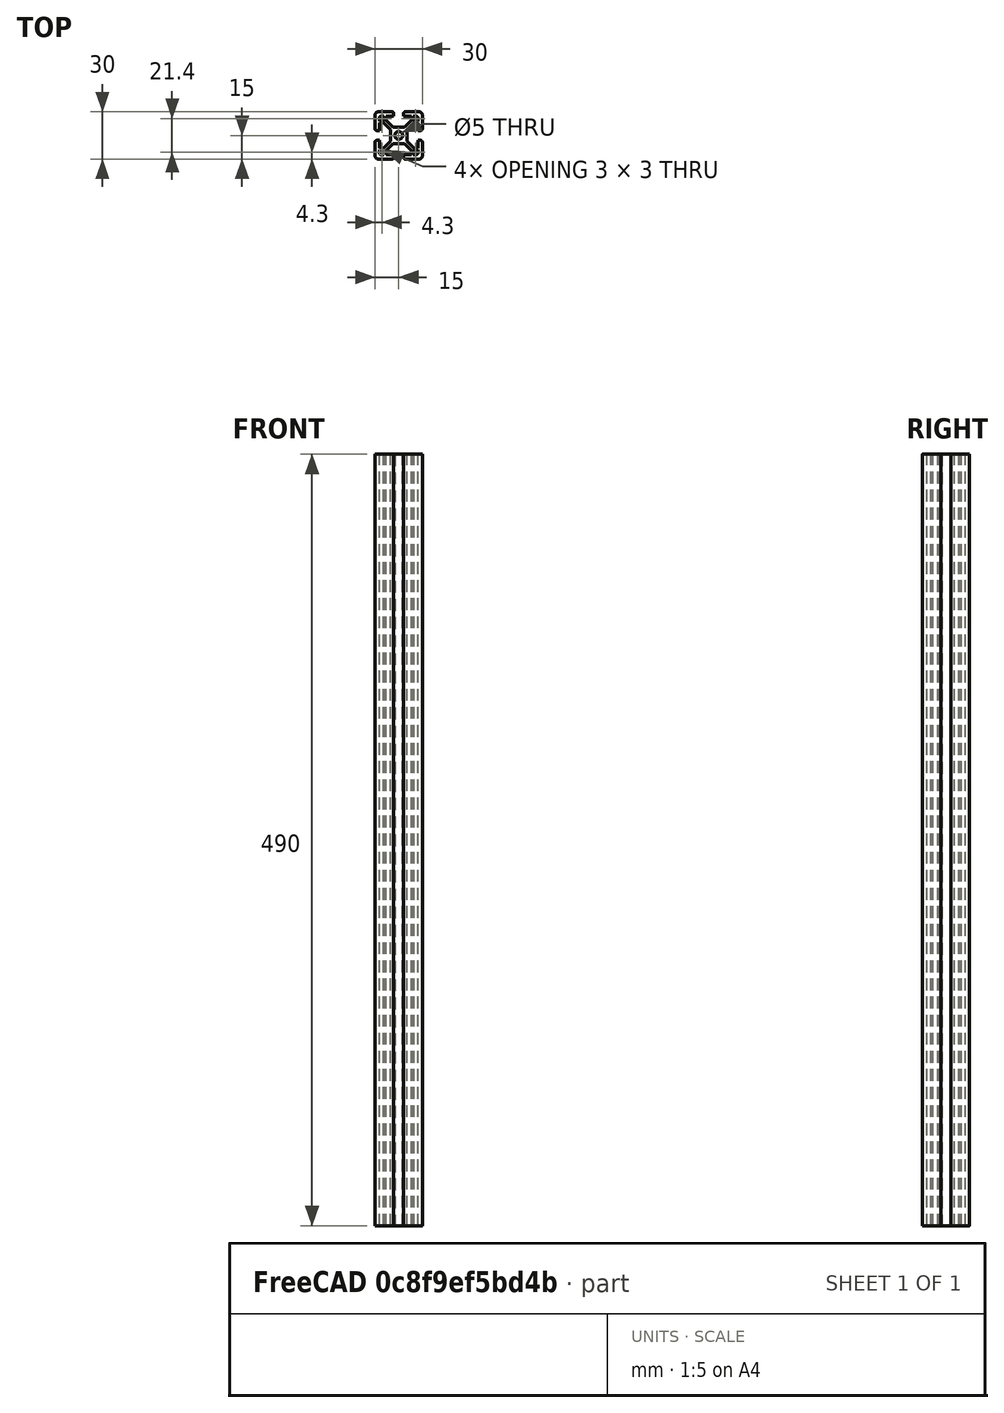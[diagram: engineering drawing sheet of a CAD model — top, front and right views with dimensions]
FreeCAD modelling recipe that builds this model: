
FCSTD DOCUMENT  (FreeCAD 0.19R18353 (Git))
Label: Profile_3030-490
License: CreativeCommons Attribution
LicenseURL: http://creativecommons.org/licenses/by/4.0/
objects: Sketcher::SketchObject×1, PartDesign::Pad×1, PartDesign::Body×1
note: 4 computed .brp shape members not serialized (recipe doc carries the construction recipe); baked Part::Feature solids carry a one-line shape summary decoded from their .brp

FEATURE [Sketcher::SketchObject] Sketch
  MapMode = 5
  Support = -> [XY_Plane]
  sketch-geometry (137):
    g0: LineSegment [constr] StartX=-5.2 StartY=5.2 StartZ=0 EndX=5.2 EndY=5.2 EndZ=0
    g1: LineSegment [constr] StartX=5.2 StartY=5.2 StartZ=0 EndX=5.2 EndY=-5.2 EndZ=0
    g2: LineSegment [constr] StartX=5.2 StartY=-5.2 StartZ=0 EndX=-5.2 EndY=-5.2 EndZ=0
    g3: LineSegment [constr] StartX=-5.2 StartY=-5.2 StartZ=0 EndX=-5.2 EndY=5.2 EndZ=0
    g4: LineSegment [constr] StartX=-15 StartY=15 StartZ=0 EndX=15 EndY=15 EndZ=0
    g5: LineSegment [constr] StartX=15 StartY=15 StartZ=0 EndX=15 EndY=-15 EndZ=0
    g6: LineSegment [constr] StartX=15 StartY=-15 StartZ=0 EndX=-15 EndY=-15 EndZ=0
    g7: LineSegment [constr] StartX=-15 StartY=-15 StartZ=0 EndX=-15 EndY=15 EndZ=0
    g8: LineSegment [constr] StartX=-12.2 StartY=12.2 StartZ=0 EndX=12.2 EndY=12.2 EndZ=0
    g9: LineSegment [constr] StartX=12.2 StartY=12.2 StartZ=0 EndX=12.2 EndY=-12.2 EndZ=0
    g10: LineSegment [constr] StartX=12.2 StartY=-12.2 StartZ=0 EndX=-12.2 EndY=-12.2 EndZ=0
    g11: LineSegment [constr] StartX=-12.2 StartY=-12.2 StartZ=0 EndX=-12.2 EndY=12.2 EndZ=0
    g12: Circle CenterX=0 CenterY=0 CenterZ=0 NormalX=0 NormalY=0 NormalZ=1 AngleXU=0 Radius=2.5
    g13: LineSegment [constr] StartX=15 StartY=15 StartZ=0 EndX=5.2 EndY=5.2 EndZ=0
    g14: LineSegment [constr] StartX=13.5151 StartY=15 StartZ=0 EndX=15 EndY=13.5151 EndZ=0
    g15: LineSegment [constr] StartX=15 StartY=13.5151 StartZ=0 EndX=5.2 EndY=3.71508 EndZ=0
    g16: LineSegment [constr] StartX=5.2 StartY=3.71508 StartZ=0 EndX=3.71508 EndY=5.2 EndZ=0
    g17: LineSegment [constr] StartX=3.71508 StartY=5.2 StartZ=0 EndX=13.5151 EndY=15 EndZ=0
    g18: LineSegment [constr] StartX=5.2 StartY=-5.2 StartZ=0 EndX=15 EndY=-15 EndZ=0
    g19: LineSegment [constr] StartX=-8.15 StartY=8.15 StartZ=0 EndX=8.15 EndY=8.15 EndZ=0
    g20: LineSegment [constr] StartX=8.15 StartY=8.15 StartZ=0 EndX=8.15 EndY=-8.15 EndZ=0
    g21: LineSegment [constr] StartX=8.15 StartY=-8.15 StartZ=0 EndX=-8.15 EndY=-8.15 EndZ=0
    g22: LineSegment [constr] StartX=-8.15 StartY=-8.15 StartZ=0 EndX=-8.15 EndY=8.15 EndZ=0
    g23: LineSegment [constr] StartX=-15 StartY=3.15 StartZ=0 EndX=15 EndY=3.15 EndZ=0
    g24: LineSegment [constr] StartX=15 StartY=3.15 StartZ=0 EndX=15 EndY=-3.15 EndZ=0
    g25: LineSegment [constr] StartX=15 StartY=-3.15 StartZ=0 EndX=-15 EndY=-3.15 EndZ=0
    g26: LineSegment [constr] StartX=-15 StartY=-3.15 StartZ=0 EndX=-15 EndY=3.15 EndZ=0
    g27: LineSegment [constr] StartX=5.2 StartY=-3.71508 StartZ=0 EndX=3.71508 EndY=-5.2 EndZ=0
    g28: LineSegment [constr] StartX=3.71508 StartY=-5.2 StartZ=0 EndX=13.5151 EndY=-15 EndZ=0
    g29: LineSegment [constr] StartX=13.5151 StartY=-15 StartZ=0 EndX=15 EndY=-13.5151 EndZ=0
    g30: LineSegment [constr] StartX=15 StartY=-13.5151 StartZ=0 EndX=5.2 EndY=-3.71508 EndZ=0
    g31: LineSegment StartX=14 StartY=3.15 StartZ=0 EndX=12.2 EndY=3.15 EndZ=0
    g32: LineSegment StartX=12.2 StartY=3.15 StartZ=0 EndX=12.2 EndY=8.15 EndZ=0
    g33: LineSegment StartX=12.2 StartY=8.15 StartZ=0 EndX=9.63492 EndY=8.15 EndZ=0
    g34: LineSegment StartX=9.63492 StartY=8.15 StartZ=0 EndX=5.2 EndY=3.71508 EndZ=0
    g35: LineSegment StartX=5.2 StartY=3.71508 StartZ=0 EndX=5.2 EndY=-3.71508 EndZ=0
    g36: LineSegment StartX=5.2 StartY=-3.71508 StartZ=0 EndX=9.63492 EndY=-8.15 EndZ=0
    g37: LineSegment StartX=9.63492 StartY=-8.15 StartZ=0 EndX=12.2 EndY=-8.15 EndZ=0
    g38: LineSegment StartX=12.2 StartY=-8.15 StartZ=0 EndX=12.2 EndY=-3.15 EndZ=0
    g39: LineSegment StartX=12.2 StartY=-3.15 StartZ=0 EndX=14 EndY=-3.15 EndZ=0
    g40: LineSegment [constr] StartX=-3.15 StartY=15 StartZ=0 EndX=3.15 EndY=15 EndZ=0
    g41: LineSegment [constr] StartX=3.15 StartY=15 StartZ=0 EndX=3.15 EndY=-15 EndZ=0
    g42: LineSegment [constr] StartX=3.15 StartY=-15 StartZ=0 EndX=-3.15 EndY=-15 EndZ=0
    g43: LineSegment [constr] StartX=-3.15 StartY=-15 StartZ=0 EndX=-3.15 EndY=15 EndZ=0
    g44: LineSegment [constr] StartX=-15 StartY=15 StartZ=0 EndX=-5.2 EndY=5.2 EndZ=0
    g45: LineSegment [constr] StartX=-5.2 StartY=-5.2 StartZ=0 EndX=-15 EndY=-15 EndZ=0
    g46: LineSegment [constr] StartX=-13.5151 StartY=15 StartZ=0 EndX=-15 EndY=13.5151 EndZ=0
    g47: LineSegment [constr] StartX=-15 StartY=13.5151 StartZ=0 EndX=-5.2 EndY=3.71508 EndZ=0
    g48: LineSegment [constr] StartX=-5.2 StartY=3.71508 StartZ=0 EndX=-3.71508 EndY=5.2 EndZ=0
    g49: LineSegment [constr] StartX=-3.71508 StartY=5.2 StartZ=0 EndX=-13.5151 EndY=15 EndZ=0
    g50: LineSegment StartX=15 StartY=4.15 StartZ=0 EndX=15 EndY=13 EndZ=0
    g51: LineSegment StartX=13 StartY=15 StartZ=0 EndX=4.15 EndY=15 EndZ=0
    g52: LineSegment StartX=3.15 StartY=14 StartZ=0 EndX=3.15 EndY=12.2 EndZ=0
    g53: LineSegment StartX=3.15 StartY=12.2 StartZ=0 EndX=8.15 EndY=12.2 EndZ=0
    g54: LineSegment StartX=8.15 StartY=12.2 StartZ=0 EndX=8.15 EndY=9.63492 EndZ=0
    g55: LineSegment StartX=8.15 StartY=9.63492 StartZ=0 EndX=3.71508 EndY=5.2 EndZ=0
    g56: LineSegment StartX=3.71508 StartY=5.2 StartZ=0 EndX=-3.71508 EndY=5.2 EndZ=0
    g57: LineSegment StartX=-3.71508 StartY=5.2 StartZ=0 EndX=-8.15 EndY=9.63492 EndZ=0
    g58: LineSegment StartX=-8.15 StartY=9.63492 StartZ=0 EndX=-8.15 EndY=12.2 EndZ=0
    g59: LineSegment StartX=-8.15 StartY=12.2 StartZ=0 EndX=-3.15 EndY=12.2 EndZ=0
    g60: LineSegment StartX=-3.15 StartY=12.2 StartZ=0 EndX=-3.15 EndY=14 EndZ=0
    g61: LineSegment StartX=-4.15 StartY=15 StartZ=0 EndX=-13 EndY=15 EndZ=0
    g62: ArcOfCircle CenterX=13 CenterY=13 CenterZ=0 NormalX=0 NormalY=0 NormalZ=1 AngleXU=0 Radius=2 StartAngle=0 EndAngle=1.5708
    g63: LineSegment [constr] StartX=-15 StartY=-13.5151 StartZ=0 EndX=-13.5151 EndY=-15 EndZ=0
    g64: LineSegment [constr] StartX=-13.5151 StartY=-15 StartZ=0 EndX=-3.71508 EndY=-5.2 EndZ=0
    g65: LineSegment [constr] StartX=-3.71508 StartY=-5.2 StartZ=0 EndX=-5.2 EndY=-3.71508 EndZ=0
    g66: LineSegment [constr] StartX=-5.2 StartY=-3.71508 StartZ=0 EndX=-15 EndY=-13.5151 EndZ=0
    g67: LineSegment StartX=-15 StartY=13 StartZ=0 EndX=-15 EndY=4.15 EndZ=0
    g68: LineSegment StartX=-14 StartY=3.15 StartZ=0 EndX=-12.2 EndY=3.15 EndZ=0
    g69: LineSegment StartX=-12.2 StartY=3.15 StartZ=0 EndX=-12.2 EndY=8.15 EndZ=0
    g70: LineSegment StartX=-9.63492 StartY=8.15 StartZ=0 EndX=-5.2 EndY=3.71508 EndZ=0
    g71: LineSegment StartX=-5.2 StartY=3.71508 StartZ=0 EndX=-5.2 EndY=-3.71508 EndZ=0
    g72: LineSegment StartX=-5.2 StartY=-3.71508 StartZ=0 EndX=-9.63492 EndY=-8.15 EndZ=0
    g73: LineSegment StartX=-12.2 StartY=-8.15 StartZ=0 EndX=-12.2 EndY=-3.15 EndZ=0
    g74: LineSegment StartX=-12.2 StartY=-3.15 StartZ=0 EndX=-14 EndY=-3.15 EndZ=0
    g75: LineSegment StartX=-15 StartY=-4.15 StartZ=0 EndX=-15 EndY=-13 EndZ=0
    g76: ArcOfCircle CenterX=14 CenterY=4.15 CenterZ=0 NormalX=0 NormalY=0 NormalZ=1 AngleXU=0 Radius=1 StartAngle=4.71239 EndAngle=6.28319
    g77: ArcOfCircle CenterX=4.15 CenterY=14 CenterZ=0 NormalX=0 NormalY=0 NormalZ=1 AngleXU=0 Radius=1 StartAngle=1.5708 EndAngle=3.14159
    g78: ArcOfCircle CenterX=-4.15 CenterY=14 CenterZ=0 NormalX=0 NormalY=0 NormalZ=1 AngleXU=0 Radius=1 StartAngle=0 EndAngle=1.5708
    g79: ArcOfCircle CenterX=-13 CenterY=13 CenterZ=0 NormalX=0 NormalY=0 NormalZ=1 AngleXU=0 Radius=2 StartAngle=1.5708 EndAngle=3.14159
    g80: ArcOfCircle CenterX=-14 CenterY=4.15 CenterZ=0 NormalX=0 NormalY=0 NormalZ=1 AngleXU=0 Radius=1 StartAngle=3.14159 EndAngle=4.71239
    g81: ArcOfCircle CenterX=-14 CenterY=-4.15 CenterZ=0 NormalX=0 NormalY=0 NormalZ=1 AngleXU=0 Radius=1 StartAngle=1.5708 EndAngle=3.14159
    g82: LineSegment StartX=15 StartY=-4.15 StartZ=0 EndX=15 EndY=-13 EndZ=0
    g83: LineSegment StartX=13 StartY=-15 StartZ=0 EndX=4.15 EndY=-15 EndZ=0
    g84: LineSegment StartX=3.15 StartY=-14 StartZ=0 EndX=3.15 EndY=-12.2 EndZ=0
    g85: LineSegment StartX=3.15 StartY=-12.2 StartZ=0 EndX=8.15 EndY=-12.2 EndZ=0
    g86: LineSegment StartX=8.15 StartY=-12.2 StartZ=0 EndX=8.15 EndY=-9.63492 EndZ=0
    g87: LineSegment StartX=8.15 StartY=-9.63492 StartZ=0 EndX=3.71508 EndY=-5.2 EndZ=0
    g88: LineSegment StartX=3.71508 StartY=-5.2 StartZ=0 EndX=-3.71508 EndY=-5.2 EndZ=0
    g89: LineSegment StartX=-3.71508 StartY=-5.2 StartZ=0 EndX=-8.15 EndY=-9.63492 EndZ=0
    g90: LineSegment StartX=-8.15 StartY=-9.63492 StartZ=0 EndX=-8.15 EndY=-12.2 EndZ=0
    g91: LineSegment StartX=-8.15 StartY=-12.2 StartZ=0 EndX=-3.15 EndY=-12.2 EndZ=0
    g92: LineSegment StartX=-3.15 StartY=-12.2 StartZ=0 EndX=-3.15 EndY=-14 EndZ=0
    g93: LineSegment StartX=-4.15 StartY=-15 StartZ=0 EndX=-13 EndY=-15 EndZ=0
    g94: ArcOfCircle CenterX=4.15 CenterY=-14 CenterZ=0 NormalX=0 NormalY=0 NormalZ=1 AngleXU=0 Radius=1 StartAngle=3.14159 EndAngle=4.71239
    g95: ArcOfCircle CenterX=-4.15 CenterY=-14 CenterZ=0 NormalX=0 NormalY=0 NormalZ=1 AngleXU=0 Radius=1 StartAngle=4.71239 EndAngle=6.28319
    g96: ArcOfCircle CenterX=-13 CenterY=-13 CenterZ=0 NormalX=0 NormalY=0 NormalZ=1 AngleXU=0 Radius=2 StartAngle=3.14159 EndAngle=4.71239
    g97: ArcOfCircle CenterX=13 CenterY=-13 CenterZ=0 NormalX=0 NormalY=0 NormalZ=1 AngleXU=0 Radius=2 StartAngle=4.71239 EndAngle=6.28319
    g98: ArcOfCircle CenterX=14 CenterY=-4.15 CenterZ=0 NormalX=0 NormalY=0 NormalZ=1 AngleXU=0 Radius=1 StartAngle=0 EndAngle=1.5708
    g99: LineSegment StartX=-12.2 StartY=8.15 StartZ=0 EndX=-9.63492 EndY=8.15 EndZ=0
    g100: LineSegment StartX=-12.2 StartY=-8.15 StartZ=0 EndX=-9.63492 EndY=-8.15 EndZ=0
    g101: LineSegment [constr] StartX=9.2 StartY=12.2 StartZ=0 EndX=12.2 EndY=12.2 EndZ=0
    g102: LineSegment [constr] StartX=12.2 StartY=12.2 StartZ=0 EndX=12.2 EndY=9.2 EndZ=0
    g103: LineSegment [constr] StartX=12.2 StartY=9.2 StartZ=0 EndX=9.2 EndY=9.2 EndZ=0
    g104: LineSegment [constr] StartX=9.2 StartY=9.2 StartZ=0 EndX=9.2 EndY=12.2 EndZ=0
    g105: LineSegment StartX=9.2 StartY=12.2 StartZ=0 EndX=11.2 EndY=12.2 EndZ=0
    g106: LineSegment StartX=12.2 StartY=9.2 StartZ=0 EndX=9.2 EndY=9.2 EndZ=0
    g107: LineSegment StartX=9.2 StartY=9.2 StartZ=0 EndX=9.2 EndY=12.2 EndZ=0
    g108: ArcOfCircle CenterX=11.2 CenterY=11.2 CenterZ=0 NormalX=0 NormalY=0 NormalZ=1 AngleXU=0 Radius=1 StartAngle=6e-16 EndAngle=1.5708
    g109: LineSegment StartX=12.2 StartY=11.2 StartZ=0 EndX=12.2 EndY=9.2 EndZ=0
    g110: LineSegment [constr] StartX=-12.2 StartY=12.2 StartZ=0 EndX=-9.2 EndY=12.2 EndZ=0
    g111: LineSegment [constr] StartX=-9.2 StartY=12.2 StartZ=0 EndX=-9.2 EndY=9.2 EndZ=0
    g112: LineSegment [constr] StartX=-9.2 StartY=9.2 StartZ=0 EndX=-12.2 EndY=9.2 EndZ=0
    g113: LineSegment [constr] StartX=-12.2 StartY=9.2 StartZ=0 EndX=-12.2 EndY=12.2 EndZ=0
    g114: ArcOfCircle CenterX=-11.2 CenterY=11.2 CenterZ=0 NormalX=0 NormalY=0 NormalZ=1 AngleXU=0 Radius=1 StartAngle=1.5708 EndAngle=3.14159
    g115: LineSegment StartX=-11.2 StartY=12.2 StartZ=0 EndX=-9.2 EndY=12.2 EndZ=0
    g116: LineSegment StartX=-9.2 StartY=12.2 StartZ=0 EndX=-9.2 EndY=9.2 EndZ=0
    g117: LineSegment StartX=-9.2 StartY=9.2 StartZ=0 EndX=-12.2 EndY=9.2 EndZ=0
    g118: LineSegment StartX=-12.2 StartY=9.2 StartZ=0 EndX=-12.2 EndY=11.2 EndZ=0
    g119: LineSegment [constr] StartX=-12.2 StartY=-9.2 StartZ=0 EndX=-9.2 EndY=-9.2 EndZ=0
    g120: LineSegment [constr] StartX=-9.2 StartY=-9.2 StartZ=0 EndX=-9.2 EndY=-12.2 EndZ=0
    g121: LineSegment [constr] StartX=-9.2 StartY=-12.2 StartZ=0 EndX=-12.2 EndY=-12.2 EndZ=0
    g122: LineSegment [constr] StartX=-12.2 StartY=-12.2 StartZ=0 EndX=-12.2 EndY=-9.2 EndZ=0
    g123: ArcOfCircle CenterX=-11.2 CenterY=-11.2 CenterZ=0 NormalX=0 NormalY=0 NormalZ=1 AngleXU=0 Radius=1 StartAngle=3.14159 EndAngle=4.71239
    g124: LineSegment StartX=-12.2 StartY=-11.2 StartZ=0 EndX=-12.2 EndY=-9.2 EndZ=0
    g125: LineSegment StartX=-12.2 StartY=-9.2 StartZ=0 EndX=-9.2 EndY=-9.2 EndZ=0
    g126: LineSegment StartX=-9.2 StartY=-9.2 StartZ=0 EndX=-9.2 EndY=-12.2 EndZ=0
    g127: LineSegment StartX=-9.2 StartY=-12.2 StartZ=0 EndX=-11.2 EndY=-12.2 EndZ=0
    g128: LineSegment [constr] StartX=9.2 StartY=-9.2 StartZ=0 EndX=12.2 EndY=-9.2 EndZ=0
    g129: LineSegment [constr] StartX=12.2 StartY=-9.2 StartZ=0 EndX=12.2 EndY=-12.2 EndZ=0
    g130: LineSegment [constr] StartX=12.2 StartY=-12.2 StartZ=0 EndX=9.2 EndY=-12.2 EndZ=0
    g131: LineSegment [constr] StartX=9.2 StartY=-12.2 StartZ=0 EndX=9.2 EndY=-9.2 EndZ=0
    g132: ArcOfCircle CenterX=11.2 CenterY=-11.2 CenterZ=0 NormalX=0 NormalY=0 NormalZ=1 AngleXU=0 Radius=1 StartAngle=4.71239 EndAngle=6.28319
    g133: LineSegment StartX=12.2 StartY=-11.2 StartZ=0 EndX=12.2 EndY=-9.2 EndZ=0
    g134: LineSegment StartX=12.2 StartY=-9.2 StartZ=0 EndX=9.2 EndY=-9.2 EndZ=0
    g135: LineSegment StartX=9.2 StartY=-9.2 StartZ=0 EndX=9.2 EndY=-12.2 EndZ=0
    g136: LineSegment StartX=9.2 StartY=-12.2 StartZ=0 EndX=11.2 EndY=-12.2 EndZ=0
  constraints (360):
    c: Coincident(g0,g1)
    c: Coincident(g1,g2)
    c: Coincident(g2,g3)
    c: Coincident(g3,g0)
    c: Horizontal(g0)
    c: Horizontal(g2)
    c: Vertical(g1)
    c: Vertical(g3)
    c: Coincident(g4,g5)
    c: Coincident(g5,g6)
    c: Coincident(g6,g7)
    c: Coincident(g7,g4)
    c: Horizontal(g4)
    c: Horizontal(g6)
    c: Vertical(g5)
    c: Vertical(g7)
    c: Coincident(g8,g9)
    c: Coincident(g9,g10)
    c: Coincident(g10,g11)
    c: Coincident(g11,g8)
    c: Horizontal(g8)
    c: Horizontal(g10)
    c: Vertical(g9)
    c: Vertical(g11)
    c: Symmetric(g1,g0,g-1)
    c: Equal(g0,g1)
    c: Symmetric(g8,g9,g-1)
    c: Equal(g8,g9)
    c: Symmetric(g4,g5,g-1)
    c: Equal(g4,g5)
    c: Diameter(g12) = 5
    c: Coincident(g12,g-1)
    c: DistanceY(g1,g1) = 10.4
    c: DistanceY(g5,g5) = 30
    c: DistanceY(g8,g4) = 2.8
    c: Coincident(g13,g4)
    c: Coincident(g13,g0)
    c: Coincident(g14,g15)
    c: Coincident(g15,g16)
    c: Coincident(g16,g17)
    c: Coincident(g17,g14)
    c: Parallel(g17,g13)
    c: Parallel(g13,g15)
    c: Angle(g17,g14) = 1.5708
    c: Angle(g16,g17) = 1.5708
    c: PointOnObject(g15,g1)
    c: PointOnObject(g16,g0)
    c: Distance(g15,g16) = 2.1
    c: PointOnObject(g14,g5)
    c: Coincident(g18,g1)
    c: Coincident(g18,g5)
    c: Coincident(g19,g20)
    c: Coincident(g20,g21)
    c: Coincident(g21,g22)
    c: Coincident(g22,g19)
    c: Horizontal(g19)
    c: Horizontal(g21)
    c: Vertical(g20)
    c: Vertical(g22)
    c: Symmetric(g20,g19,g-1)
    c: Equal(g19,g20)
    c: DistanceY(g20,g20) = 16.3
    c: Coincident(g23,g24)
    c: Coincident(g24,g25)
    c: Coincident(g25,g26)
    c: Coincident(g26,g23)
    c: Horizontal(g23)
    c: Horizontal(g25)
    c: Vertical(g24)
    c: Vertical(g26)
    c: Symmetric(g24,g23,g-1)
    c: DistanceY(g25,g23) = 6.3
    c: PointOnObject(g25,g7)
    c: Coincident(g27,g28)
    c: Coincident(g28,g29)
    c: Coincident(g29,g30)
    c: Coincident(g30,g27)
    c: Equal(g28,g18)
    c: Equal(g18,g30)
    c: PointOnObject(g27,g1)
    c: PointOnObject(g27,g2)
    c: PointOnObject(g28,g6)
    c: PointOnObject(g29,g5)
    c: Angle(g30,g29) = 1.5708
    c: Distance(g29,g28) = 2.1
    c: Horizontal(g31)
    c: Coincident(g31,g32)
    c: Vertical(g32)
    c: Coincident(g32,g33)
    c: Horizontal(g33)
    c: Coincident(g33,g34)
    c: Coincident(g34,g35)
    c: Coincident(g35,g36)
    c: Coincident(g36,g37)
    c: Coincident(g37,g38)
    c: Coincident(g38,g39)
    c: Symmetric(g34,g35,g-1)
    c: Symmetric(g38,g31,g-1)
    c: Symmetric(g37,g32,g-1)
    c: Coincident(g35,g27)
    c: PointOnObject(g32,g9)
    c: PointOnObject(g33,g15)
    c: Symmetric(g36,g33,g-1)
    c: Coincident(g40,g41)
    c: Coincident(g41,g42)
    c: Coincident(g42,g43)
    c: Coincident(g43,g40)
    c: Horizontal(g42)
    c: Vertical(g43)
    c: Symmetric(g41,g40,g-1)
    c: DistanceX(g42,g41) = 6.3
    c: PointOnObject(g41,g6)
    c: Coincident(g44,g4)
    c: Coincident(g44,g0)
    c: Coincident(g45,g2)
    c: Coincident(g45,g6)
    c: Coincident(g46,g47)
    c: Coincident(g47,g48)
    c: Coincident(g48,g49)
    c: Coincident(g49,g46)
    c: Parallel(g49,g47)
    c: Parallel(g47,g44)
    c: Parallel(g46,g48)
    c: Symmetric(g46,g46,g44)
    c: Distance(g46,g46) = 2.1
    c: PointOnObject(g46,g7)
    c: PointOnObject(g47,g3)
    c: Horizontal(g33,g19)
    c: Vertical(g50)
    c: Horizontal(g51)
    c: Coincident(g52,g53)
    c: Horizontal(g53)
    c: Coincident(g53,g54)
    c: Vertical(g54)
    c: Coincident(g54,g55)
    c: Coincident(g55,g56)
    c: Coincident(g56,g57)
    c: Coincident(g57,g58)
    c: Vertical(g58)
    c: Coincident(g58,g59)
    c: Horizontal(g59)
    c: Coincident(g59,g60)
    c: Vertical(g60)
    c: Horizontal(g61)
    c: Symmetric(g55,g56,g-2)
    c: Symmetric(g57,g54,g-2)
    c: Symmetric(g59,g52,g-2)
    c: Vertical(g52)
    c: Coincident(g55,g16)
    c: PointOnObject(g54,g17)
    c: Equal(g37,g54)
    c: PointOnObject(g53,g8)
    c: Tangent(g51,g62) = -1.5708
    c: Tangent(g50,g62) = -1.5708
    c: Radius(g62) = 2
    c: Coincident(g63,g64)
    c: Coincident(g64,g65)
    c: Coincident(g65,g66)
    c: Coincident(g66,g63)
    c: Parallel(g64,g66)
    c: Parallel(g66,g45)
    c: Distance(g63,g63) = 2.1
    c: Parallel(g65,g63)
    c: Symmetric(g64,g65,g45)
    c: PointOnObject(g64,g2)
    c: PointOnObject(g63,g7)
    c: Horizontal(g68)
    c: Coincident(g68,g69)
    c: Vertical(g69)
    c: Coincident(g70,g71)
    c: Coincident(g71,g72)
    c: Vertical(g73)
    c: Coincident(g73,g74)
    c: Horizontal(g74)
    c: Symmetric(g70,g71,g-1)
    c: Coincident(g70,g47)
    c: Tangent(g50,g76) = -1.5708
    c: Tangent(g31,g76) = 1.5708
    c: Radius(g76) = 1
    c: PointOnObject(g50,g5)
    c: Tangent(g51,g77) = -1.5708
    c: Tangent(g52,g77) = -1.5708
    c: Equal(g77,g76)
    c: PointOnObject(g51,g4)
    c: Symmetric(g40,g40,g-2)
    c: PointOnObject(g59,g43)
    c: Tangent(g61,g78) = -1.5708
    c: Tangent(g60,g78) = -1.5708
    c: Equal(g78,g77)
    c: Horizontal(g39)
    c: Tangent(g61,g79) = -1.5708
    c: Tangent(g67,g79) = -1.5708
    c: Equal(g79,g62)
    c: Vertical(g67)
    c: PointOnObject(g61,g4)
    c: Tangent(g67,g80) = -1.5708
    c: Tangent(g68,g80) = -1.5708
    c: Equal(g80,g78)
    c: PointOnObject(g67,g7)
    c: Tangent(g74,g81) = -1.5708
    c: Tangent(g75,g81) = -1.5708
    c: Equal(g80,g81)
    c: PointOnObject(g73,g25)
    c: PointOnObject(g84,g10)
    c: Coincident(g84,g85)
    c: PointOnObject(g85,g10)
    c: Coincident(g85,g86)
    c: PointOnObject(g86,g28)
    c: Vertical(g86)
    c: Coincident(g86,g87)
    c: Coincident(g87,g88)
    c: Coincident(g88,g89)
    c: Coincident(g89,g90)
    c: PointOnObject(g90,g10)
    c: Coincident(g90,g91)
    c: PointOnObject(g91,g10)
    c: Coincident(g91,g92)
    c: Vertical(g92)
    c: Horizontal(g93)
    c: Vertical(g90)
    c: Symmetric(g89,g86,g-2)
    c: Vertical(g84)
    c: PointOnObject(g91,g43)
    c: Symmetric(g88,g87,g-2)
    c: Coincident(g88,g64)
    c: Vertical(g86,g20)
    c: PointOnObject(g68,g23)
    c: Vertical(g75)
    c: Tangent(g84,g94) = 1.5708
    c: Tangent(g83,g94) = 1.5708
    c: Tangent(g92,g95) = 1.5708
    c: Tangent(g93,g95) = 1.5708
    c: Equal(g95,g94)
    c: Equal(g94,g81)
    c: PointOnObject(g84,g41)
    c: Horizontal(g83)
    c: Tangent(g75,g96) = -1.5708
    c: Tangent(g93,g96) = 1.5708
    c: Tangent(g83,g97) = 1.5708
    c: Tangent(g82,g97) = 1.5708
    c: Equal(g79,g96)
    c: Equal(g96,g97)
    c: Vertical(g82)
    c: PointOnObject(g75,g7)
    c: PointOnObject(g93,g6)
    c: PointOnObject(g83,g6)
    c: Tangent(g39,g98) = 1.5708
    c: Tangent(g82,g98) = 1.5708
    c: Equal(g98,g76)
    c: PointOnObject(g38,g25)
    c: PointOnObject(g82,g5)
    c: Horizontal(g99)
    c: Horizontal(g100)
    c: Equal(g99,g58)
    c: Coincident(g69,g99)
    c: Coincident(g70,g99)
    c: PointOnObject(g73,g11)
    c: Equal(g100,g90)
    c: Coincident(g73,g100)
    c: Coincident(g72,g100)
    c: PointOnObject(g72,g66)
    c: Horizontal(g70,g19)
    c: PointOnObject(g70,g47)
    c: Coincident(g101,g102)
    c: Coincident(g102,g103)
    c: Coincident(g103,g104)
    c: Coincident(g104,g101)
    c: Horizontal(g101)
    c: Horizontal(g103)
    c: Vertical(g102)
    c: Vertical(g104)
    c: Equal(g102,g101)
    c: DistanceY(g102,g102) = 3
    c: Coincident(g101,g8)
    c: Coincident(g106,g107)
    c: Coincident(g107,g105)
    c: Horizontal(g105)
    c: Vertical(g107)
    c: Coincident(g106,g103)
    c: PointOnObject(g108,g13)
    c: Horizontal(g108,g108)
    c: Vertical(g108,g108)
    c: Radius(g108) = 1
    c: PointOnObject(g108,g9)
    c: Coincident(g105,g108)
    c: Coincident(g106,g102)
    c: Coincident(g108,g109)
    c: Coincident(g109,g106)
    c: Coincident(g110,g111)
    c: Coincident(g111,g112)
    c: Coincident(g112,g113)
    c: Coincident(g113,g110)
    c: Horizontal(g110)
    c: Horizontal(g112)
    c: Vertical(g111)
    c: Vertical(g113)
    c: Equal(g111,g112)
    c: DistanceY(g111,g111) = 3
    c: Coincident(g110,g8)
    c: PointOnObject(g114,g44)
    c: PointOnObject(g114,g8)
    c: PointOnObject(g114,g11)
    c: Horizontal(g114,g114)
    c: Tangent(g114,g115) = 1.5708
    c: Coincident(g115,g116)
    c: Coincident(g116,g111)
    c: Vertical(g116)
    c: Coincident(g116,g117)
    c: Coincident(g117,g112)
    c: Coincident(g117,g118)
    c: Coincident(g118,g114)
    c: Equal(g108,g114)
    c: Coincident(g119,g120)
    c: Coincident(g120,g121)
    c: Coincident(g121,g122)
    c: Coincident(g122,g119)
    c: Horizontal(g119)
    c: Horizontal(g121)
    c: Vertical(g120)
    c: Vertical(g122)
    c: Equal(g120,g119)
    c: DistanceY(g120,g120) = 3
    c: Coincident(g121,g10)
    c: PointOnObject(g123,g45)
    c: PointOnObject(g123,g10)
    c: PointOnObject(g123,g11)
    c: Vertical(g123,g123)
    c: Tangent(g123,g124) = 1.5708
    c: Coincident(g124,g125)
    c: Coincident(g125,g119)
    c: Horizontal(g125)
    c: Coincident(g125,g126)
    c: Coincident(g126,g120)
    c: Coincident(g126,g127)
    c: Coincident(g127,g123)
    c: Radius(g123) = 1
    c: Coincident(g128,g129)
    c: Coincident(g129,g130)
    c: Coincident(g130,g131)
    c: Coincident(g131,g128)
    c: Horizontal(g128)
    c: Horizontal(g130)
    c: Vertical(g129)
    c: Vertical(g131)
    c: Equal(g128,g131)
    c: DistanceX(g128,g128) = 3
    c: Coincident(g129,g9)
    c: PointOnObject(g132,g18)
    c: PointOnObject(g132,g9)
    c: PointOnObject(g132,g10)
    c: Vertical(g132,g132)
    c: Tangent(g132,g133) = -1.5708
    c: Coincident(g133,g134)
    c: Coincident(g134,g128)
    c: Horizontal(g134)
    c: Coincident(g134,g135)
    c: Coincident(g135,g130)
    c: Coincident(g135,g136)
    c: Coincident(g136,g132)
    c: Radius(g132) = 1
FEATURE [PartDesign::Pad] Pad
  Length = 490
  Length2 = 100
  Midplane = true
  Profile = -> Sketch
  Refine = true
  Type = 0
FEATURE [PartDesign::Body] Body
  Group = -> [Sketch,Pad]
  Origin = -> Origin
  Tip = -> Pad
